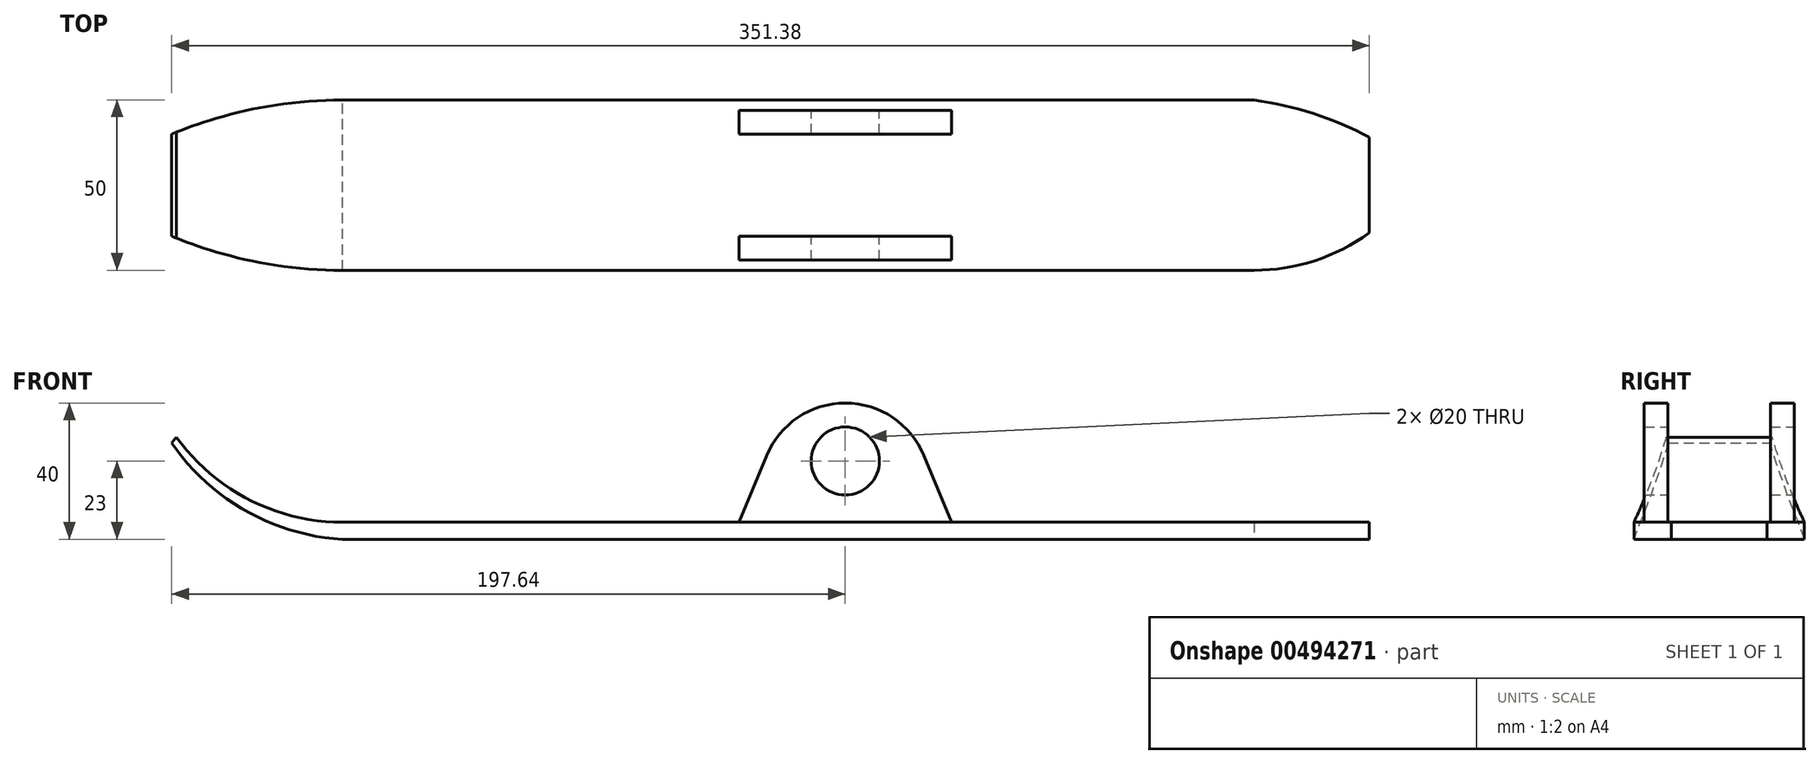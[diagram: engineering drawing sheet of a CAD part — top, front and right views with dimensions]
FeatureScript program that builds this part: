
annotation { "Feature Type Name" : "Feature", "Feature Type Description" : "" }
export const myFeature = defineFeature(function(context is Context, id is Id, definition is map)
    precondition{}
    {
        {
            var Q0;
            Q0=qCreatedBy(makeId("Front.planeOp"),FACE);
            var sketch = newSketch(context, id + "F0", { "sketchPlane" : qUnion([Q0])});
            skLineSegment(sketch, "E0", {"start": v(-147.46, 0) * mm, "end": v(153.74, 0) * mm});
            skArc(sketch, "E1", {"start": v(-196.26, 25) * mm, "mid": v(-174.87, 6.61) * mm, "end": v(-147.46, 0) * mm});
            skLineSegment(sketch, "E2.0", {"start": v(-147.46, -5) * mm, "end": v(153.74, -5) * mm});
            skArc(sketch, "E2.1", {"start": v(-197.64, 23.33) * mm, "mid": v(-175.85, 3.32) * mm, "end": v(-147.46, -5) * mm});
            skLineSegment(sketch, "E3", {"start": v(153.74, 0) * mm, "end": v(153.74, -5) * mm});
            skLineSegment(sketch, "E4", {"start": v(-197.64, 23.33) * mm, "end": v(-196.26, 25) * mm});
            skArc(sketch, "E5", {"start": v(23.1, 19.57) * mm, "mid": v(0, 35) * mm, "end": v(-23.1, 19.57) * mm});
            skLineSegment(sketch, "E6", {"start": v(-23.1, 19.57) * mm, "end": v(-31.2, 0) * mm});
            skLineSegment(sketch, "E7", {"start": v(23.1, 19.57) * mm, "end": v(31.2, 0) * mm});
            skCircle(sketch, "E8", {"center": v(0, 18) * mm, "radius": 10 * mm});
            skSolve(sketch);
        }
        {
            var Q0;
            Q0 = qSketchRegion(id + "F0", true);
            extrude(context, id + "F1", {"entities" : qUnion([Q0]), "endBound" : BoundingType.SYMMETRIC, "depth" : 50 * mm});
        }
        {
            var Q0;
            Q0=qCreatedBy(makeId("Right.planeOp"),FACE);
            var sketch = newSketch(context, id + "F2", { "sketchPlane" : qUnion([Q0])});
            skLineSegment(sketch, "E9", {"start": v(-15, 40.77) * mm, "end": v(-15, 0) * mm});
            skLineSegment(sketch, "E10", {"start": v(-15, 0) * mm, "end": v(15, 0) * mm});
            skLineSegment(sketch, "E11", {"start": v(15, 0) * mm, "end": v(15, 40.77) * mm});
            skLineSegment(sketch, "E12", {"start": v(15, 40.77) * mm, "end": v(-15, 40.77) * mm});
            skLineSegment(sketch, "E13.bottom", {"start": v(-25, 0) * mm, "end": v(-22, 0) * mm});
            skLineSegment(sketch, "E13.top", {"start": v(-25, 40.77) * mm, "end": v(-22, 40.77) * mm});
            skLineSegment(sketch, "E13.left", {"start": v(-25, 0) * mm, "end": v(-25, 40.77) * mm});
            skLineSegment(sketch, "E13.right", {"start": v(-22, 0) * mm, "end": v(-22, 40.77) * mm});
            skLineSegment(sketch, "E14.bottom", {"start": v(25, 0) * mm, "end": v(22, 0) * mm});
            skLineSegment(sketch, "E14.top", {"start": v(25, 40.77) * mm, "end": v(22, 40.77) * mm});
            skLineSegment(sketch, "E14.left", {"start": v(25, 0) * mm, "end": v(25, 40.77) * mm});
            skLineSegment(sketch, "E14.right", {"start": v(22, 0) * mm, "end": v(22, 40.77) * mm});
            skSolve(sketch);
        }
        {
            var Q0;
            Q0 = qSketchRegion(id + "F2", true);
            extrude(context, id + "F3", {"entities" : qUnion([Q0]), "operationType" : NewBodyOperationType.REMOVE, "endBound" : BoundingType.SYMMETRIC, "oppositeDirection" : true, "depth" : 80 * mm});
        }
        {
            var Q0;
            Q0=makeQuery(id+"F1.opExtrude","SWEPT_FACE",FACE,{"disambiguationData":[OSD([sQuery(id+"F0.wireOp",EDGE,"E2.0")])]});
            var sketch = newSketch(context, id + "F4", { "sketchPlane" : qUnion([Q0])});
            skArc(sketch, "E15", {"start": v(-147.46, 25) * mm, "mid": v(-173.04, 22.48) * mm, "end": v(-197.64, 15) * mm});
            skArc(sketch, "E16", {"start": v(-197.64, -15) * mm, "mid": v(-173.04, -22.48) * mm, "end": v(-147.46, -25) * mm});
            skLineSegment(sketch, "E17", {"start": v(-147.46, -25) * mm, "end": v(-197.64, -25) * mm});
            skLineSegment(sketch, "E18", {"start": v(-197.64, -25) * mm, "end": v(-197.64, -15) * mm});
            skLineSegment(sketch, "E19", {"start": v(-197.64, 15) * mm, "end": v(-197.64, 25) * mm});
            skLineSegment(sketch, "E20", {"start": v(-197.64, 25) * mm, "end": v(-147.46, 25) * mm});
            skArc(sketch, "E21", {"start": v(119.95, -25) * mm, "mid": v(137.34, -21.03) * mm, "end": v(153.74, -14.03) * mm});
            skLineSegment(sketch, "E22.0", {"start": v(153.74, 25) * mm, "end": v(153.74, 14.03) * mm});
            skLineSegment(sketch, "E23.0", {"start": v(119.95, -25) * mm, "end": v(153.74, -25) * mm});
            skLineSegment(sketch, "E24.0", {"start": v(119.95, 25) * mm, "end": v(153.74, 25) * mm});
            skPoint(sketch, "E25.orphan", {"position": v(-147.46, -25) * mm});
            skPoint(sketch, "E26.orphan", {"position": v(-147.46, 25) * mm});
            skLineSegment(sketch, "E27.trimOffspring", {"start": v(153.74, -14.03) * mm, "end": v(153.74, -25) * mm});
            skArc(sketch, "E28", {"start": v(153.74, 14.03) * mm, "mid": v(137.71, 22.19) * mm, "end": v(119.95, 25) * mm});
            skSolve(sketch);
        }
        {
            var Q0;
            Q0 = qSketchRegion(id + "F4", true);
            extrude(context, id + "F5", {"entities" : qUnion([Q0]), "operationType" : NewBodyOperationType.REMOVE, "endBound" : BoundingType.THROUGH_ALL, "oppositeDirection" : true, "depth" : 25 * mm});
        }
    });
